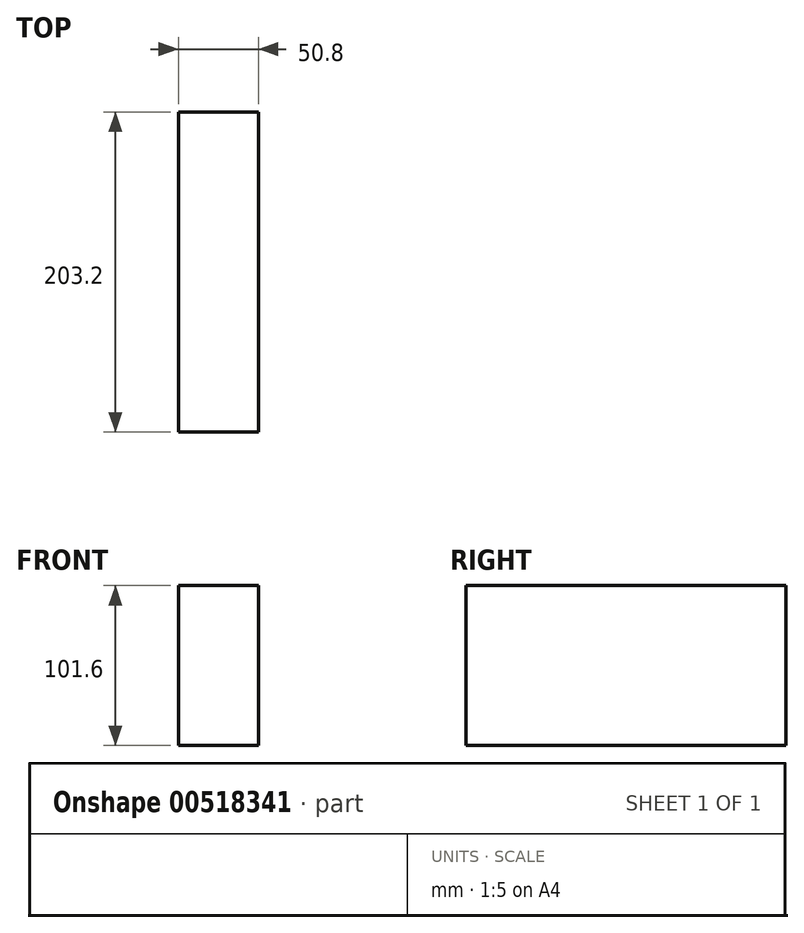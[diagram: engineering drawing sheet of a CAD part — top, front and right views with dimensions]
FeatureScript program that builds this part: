
annotation { "Feature Type Name" : "Feature", "Feature Type Description" : "" }
export const myFeature = defineFeature(function(context is Context, id is Id, definition is map)
    precondition{}
    {
        {
            var Q0;
            Q0=qCreatedBy(makeId("Top.planeOp"),FACE);
            var sketch = newSketch(context, id + "F0", { "sketchPlane" : qUnion([Q0])});
            skLineSegment(sketch, "E0.bottom", {"start": v(-25.4, 101.6) * mm, "end": v(25.4, 101.6) * mm});
            skLineSegment(sketch, "E0.top", {"start": v(-25.4, -101.6) * mm, "end": v(25.4, -101.6) * mm});
            skLineSegment(sketch, "E0.left", {"start": v(-25.4, 101.6) * mm, "end": v(-25.4, -101.6) * mm});
            skLineSegment(sketch, "E0.right", {"start": v(25.4, 101.6) * mm, "end": v(25.4, -101.6) * mm});
            skPoint(sketch, "E0.middle", {"position": v(0, 0) * mm});
            skSolve(sketch);
        }
        {
            var Q0;
            Q0=makeQuery(id+"F0.imprint","IMPRINT",FACE,{"disambiguationData":[TD([[makeQuery(id+"F0.imprint","IMPRINT",EDGE,{"derivedFrom":sQuery(id+"F0.wireOp",EDGE,"E0.bottom")}),-1.0]])]});
            extrude(context, id + "F1", {"entities" : qUnion([Q0]), "depth" : 101.6 * mm, "offsetDistance" : 25.4 * mm});
        }
    });
